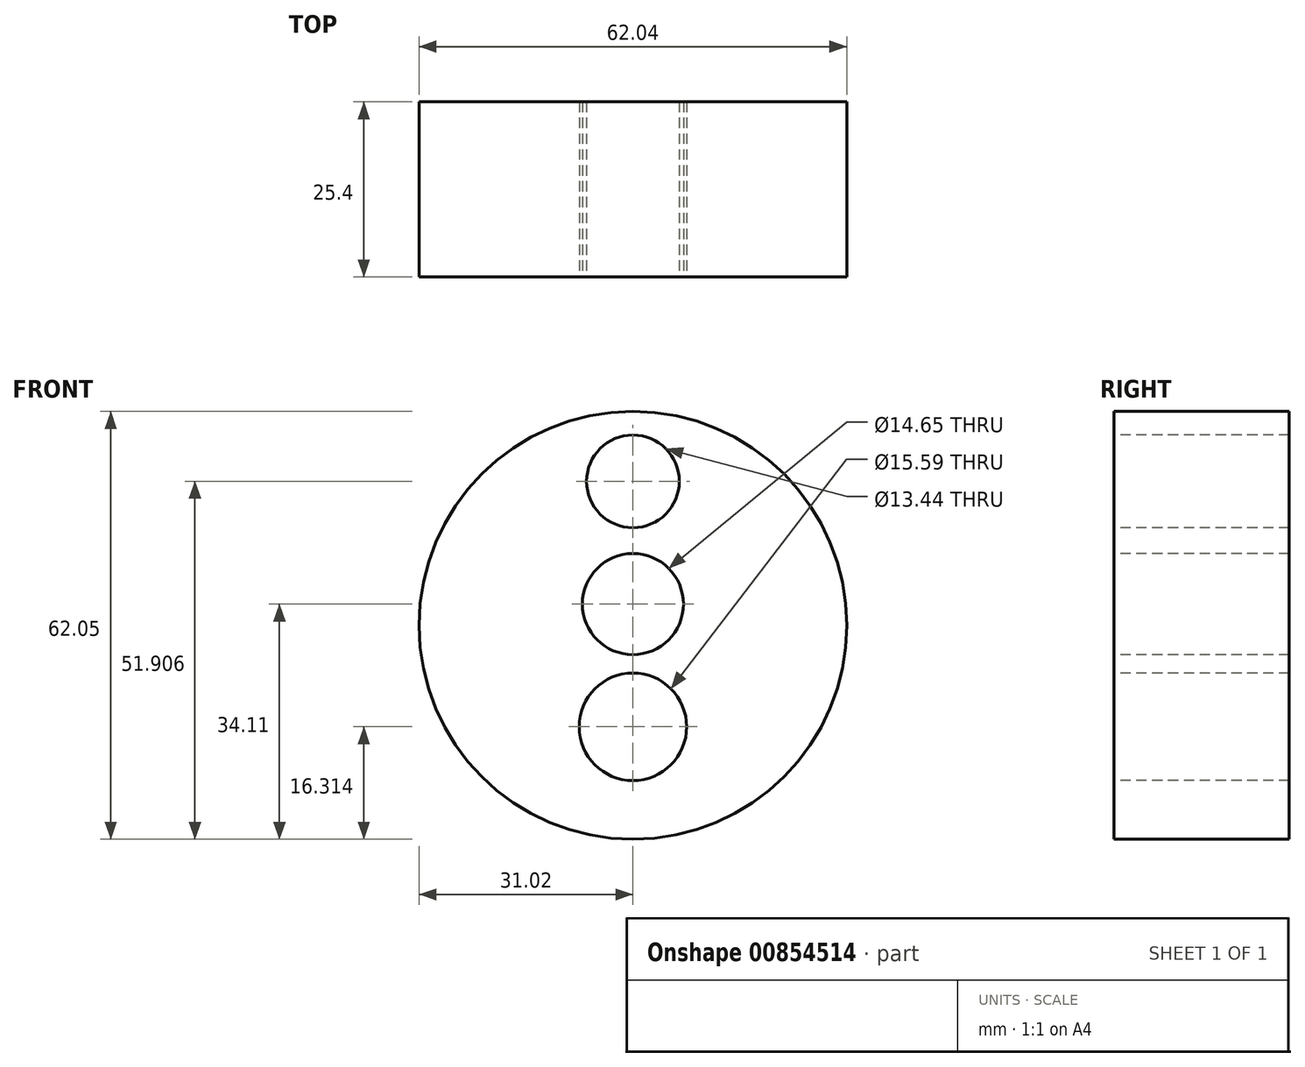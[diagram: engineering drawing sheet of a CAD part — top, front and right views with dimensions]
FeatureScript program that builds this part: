
annotation { "Feature Type Name" : "Feature", "Feature Type Description" : "" }
export const myFeature = defineFeature(function(context is Context, id is Id, definition is map)
    precondition{}
    {
        {
            var Q0;
            Q0=qCreatedBy(makeId("Front.planeOp"),FACE);
            var sketch = newSketch(context, id + "F0", { "sketchPlane" : qUnion([Q0])});
            skCircle(sketch, "E0", {"center": v(0, -3.09) * mm, "radius": 31.02 * mm});
            skSolve(sketch);
        }
        {
            var Q0;
            Q0 = qSketchRegion(id + "F0", true);
            extrude(context, id + "F1", {"entities" : qUnion([Q0]), "depth" : 25.4 * mm, "offsetDistance" : 25.4 * mm});
        }
        {
            var Q0;
            Q0=makeQuery(id+"F1.opExtrude","CAP_FACE",FACE,{"disambiguationData":[OSD([sQuery(id+"F0.wireOp",EDGE,"E0")])],"isStart":false});
            var sketch = newSketch(context, id + "F2", { "sketchPlane" : qUnion([Q0])});
            skCircle(sketch, "E1", {"center": v(0, 0) * mm, "radius": 7.33 * mm});
            skCircle(sketch, "E2", {"center": v(0, -17.8) * mm, "radius": 7.8 * mm});
            skCircle(sketch, "E3", {"center": v(0, 17.8) * mm, "radius": 6.72 * mm});
            skSolve(sketch);
        }
        {
            var Q0;
            Q0 = qSketchRegion(id + "F2", true);
            extrude(context, id + "F3", {"entities" : qUnion([Q0]), "operationType" : NewBodyOperationType.REMOVE, "endBound" : BoundingType.THROUGH_ALL, "oppositeDirection" : true, "depth" : 25.4 * mm, "offsetDistance" : 25.4 * mm});
        }
    });
